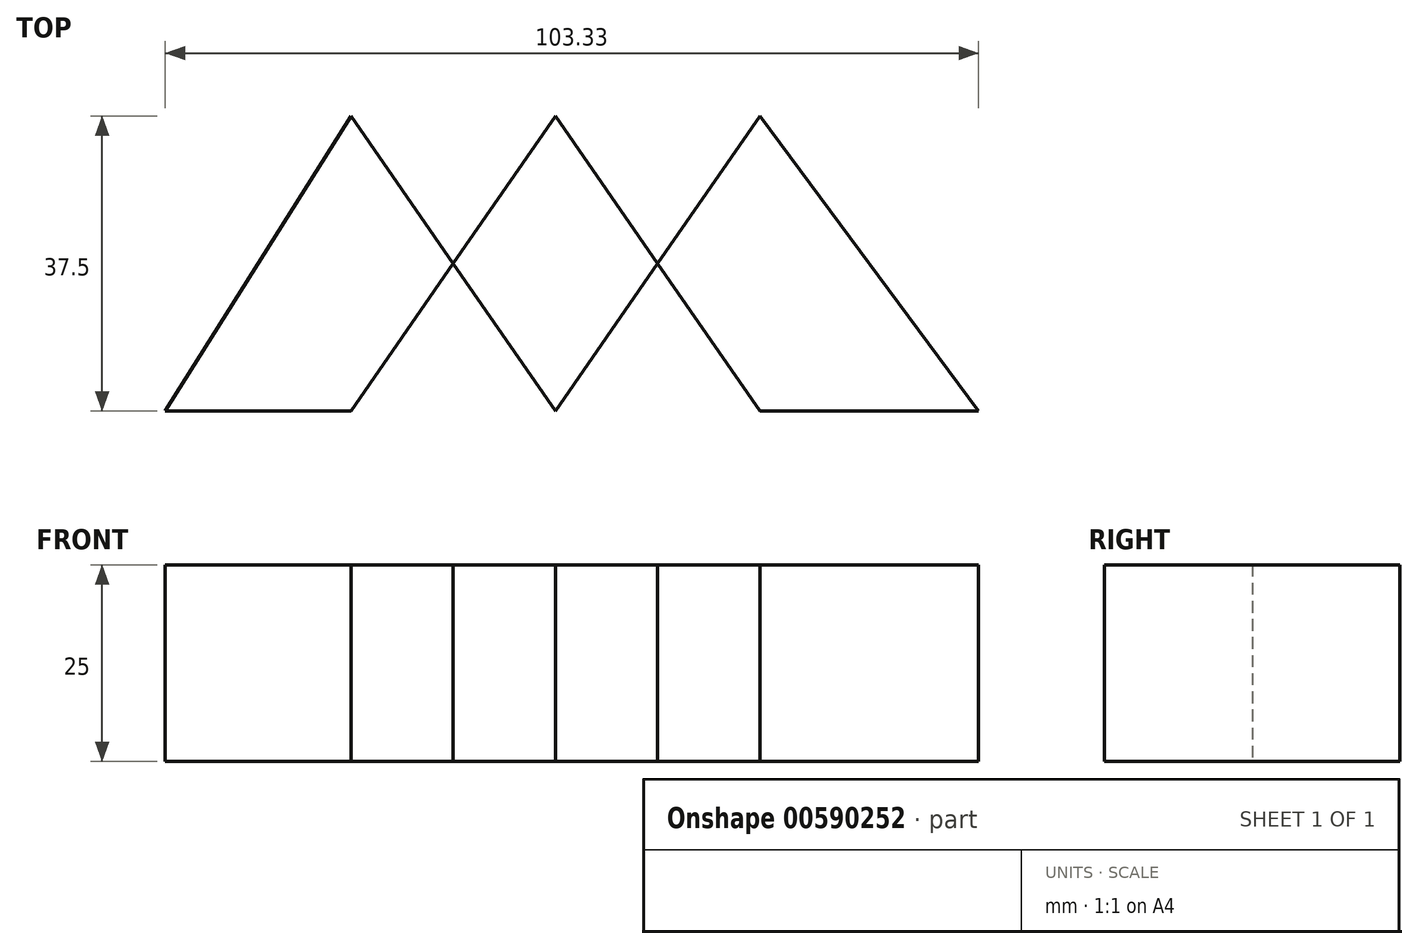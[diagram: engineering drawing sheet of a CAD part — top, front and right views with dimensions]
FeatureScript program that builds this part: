
annotation { "Feature Type Name" : "Feature", "Feature Type Description" : "" }
export const myFeature = defineFeature(function(context is Context, id is Id, definition is map)
    precondition{}
    {
        {
            var Q0;
            Q0=qCreatedBy(makeId("Top.planeOp"),FACE);
            var sketch = newSketch(context, id + "F0", { "sketchPlane" : qUnion([Q0])});
            skLineSegment(sketch, "E0", {"start": v(-49.58, 0) * mm, "end": v(-25.97, 37.5) * mm});
            skLineSegment(sketch, "E1", {"start": v(-25.97, 37.5) * mm, "end": v(0, 0) * mm});
            skLineSegment(sketch, "E2", {"start": v(0, 0) * mm, "end": v(25.97, 37.5) * mm});
            skLineSegment(sketch, "E3", {"start": v(25.97, 37.5) * mm, "end": v(53.75, 0) * mm});
            skLineSegment(sketch, "E4", {"start": v(53.75, 0) * mm, "end": v(25.97, 0) * mm});
            skLineSegment(sketch, "E5", {"start": v(25.97, 0) * mm, "end": v(0, 37.5) * mm});
            skLineSegment(sketch, "E6", {"start": v(0, 37.5) * mm, "end": v(-25.97, 0) * mm});
            skLineSegment(sketch, "E7", {"start": v(-25.97, 0) * mm, "end": v(-49.58, 0) * mm});
            skLineSegment(sketch, "E8.bottom", {"start": v(25.97, 37.5) * mm, "end": v(-25.97, 37.5) * mm, "construction": true});
            skLineSegment(sketch, "E8.top", {"start": v(25.97, 0) * mm, "end": v(-25.97, 0) * mm, "construction": true});
            skLineSegment(sketch, "E8.left", {"start": v(25.97, 37.5) * mm, "end": v(25.97, 0) * mm, "construction": true});
            skLineSegment(sketch, "E8.right", {"start": v(-25.97, 37.5) * mm, "end": v(-25.97, 0) * mm, "construction": true});
            skLineSegment(sketch, "E9", {"start": v(0, 37.5) * mm, "end": v(0, 0) * mm, "construction": true});
            skSolve(sketch);
        }
        {
            var Q0;
            Q0 = qSketchRegion(id + "F0", true);
            extrude(context, id + "F1", {"entities" : qUnion([Q0]), "depth" : 25 * mm, "offsetDistance" : 25 * mm});
        }
    });
